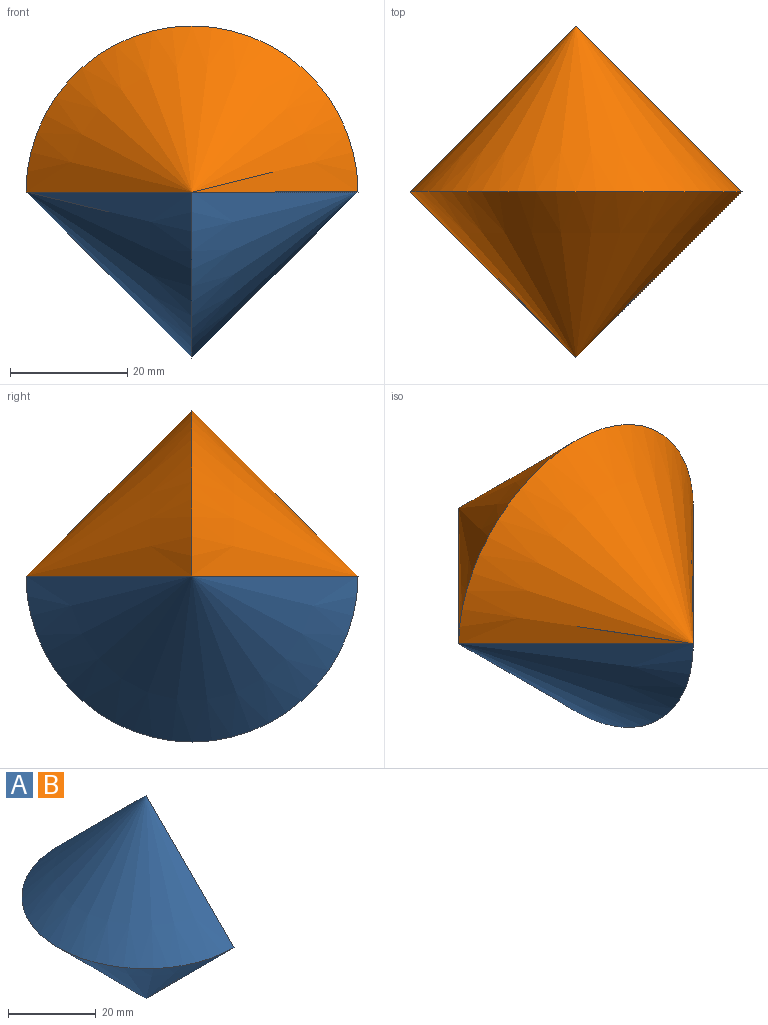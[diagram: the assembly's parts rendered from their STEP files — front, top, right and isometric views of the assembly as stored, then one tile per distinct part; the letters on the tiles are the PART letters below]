
ASSEMBLY  parts=2 mates=1
PART A: 3 faces, bbox 28.3x56.6x56.6 mm
  f0: cone r=0mm half-angle=45deg, axis (0,0,-1), area 1777.2mm2, adj f1,f2
  f1: cone r=28.28mm half-angle=45deg, axis (0,0,1), area 1777.2mm2, adj f0,f2
  f2: plane 56.57x56.57mm, normal (1,0,0), area 1600mm2, adj f0,f1
PART B: same geometry as A
PLACE A rot(axis=(0,-1,0),90deg) t=(0,0,0)mm fixed
PLACE B rot(axis=(-0.58,0.58,0.58),120deg) t=(0,0,0)mm
MATE fastened A.f2 <-> B.f2  axis (0,0,1) through (0,0,0)mm
